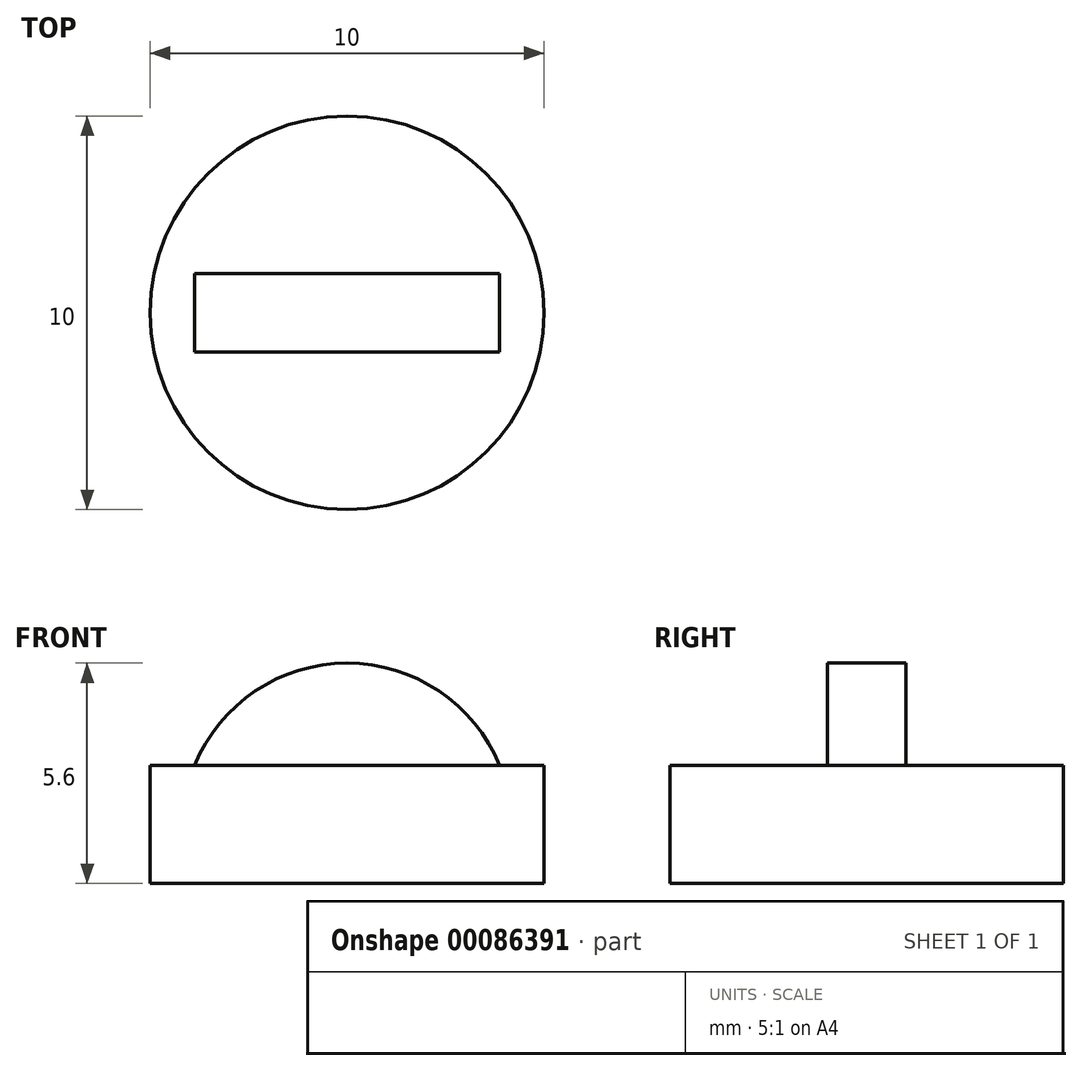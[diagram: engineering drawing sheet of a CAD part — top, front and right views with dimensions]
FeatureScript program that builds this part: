
annotation { "Feature Type Name" : "Feature", "Feature Type Description" : "" }
export const myFeature = defineFeature(function(context is Context, id is Id, definition is map)
    precondition{}
    {
        {
            assignVariable(context, id + "F0", {"name" : "H", "anyValue" : 3});
        }
        {
            var Q0;
            Q0=qCreatedBy(makeId("Top.planeOp"),FACE);
            var sketch = newSketch(context, id + "F1", { "sketchPlane" : qUnion([Q0])});
            skCircle(sketch, "E0", {"center": v(0, 0) * mm, "radius": 5 * mm});
            skCircle(sketch, "E1", {"center": v(0, 0) * mm, "radius": 4 * mm, "construction": true});
            skLineSegment(sketch, "E2.bottom", {"start": v(-3.87, 1) * mm, "end": v(3.87, 1) * mm, "construction": true});
            skLineSegment(sketch, "E2.top", {"start": v(-3.87, -1) * mm, "end": v(3.87, -1) * mm, "construction": true});
            skLineSegment(sketch, "E2.left", {"start": v(-3.87, 1) * mm, "end": v(-3.87, -1) * mm, "construction": true});
            skLineSegment(sketch, "E2.right", {"start": v(3.87, 1) * mm, "end": v(3.87, -1) * mm, "construction": true});
            skSolve(sketch);
        }
        {
            var Q0;
            Q0=makeQuery(id+"F1.imprint","IMPRINT",FACE,{"disambiguationData":[TD([[makeQuery(id+"F1.imprint","IMPRINT",EDGE,{"derivedFrom":sQuery(id+"F1.wireOp",EDGE,"E0")}),1.0]])]});
            extrude(context, id + "F2", {"entities" : qUnion([Q0]), "oppositeDirection" : true, "depth" : (getVariable(context, 'H')) * mm});
        }
        {
            var Q0;
            Q0=qCreatedBy(makeId("Front.planeOp"),FACE);
            var sketch = newSketch(context, id + "F3", { "sketchPlane" : qUnion([Q0])});
            skPoint(sketch, "E3.0", {"position": v(-3.87, 0) * mm});
            skPoint(sketch, "E4.0", {"position": v(3.87, 0) * mm});
            skLineSegment(sketch, "E5.0", {"start": v(-3.87, 0) * mm, "end": v(3.87, 0) * mm});
            skPoint(sketch, "E6.orphan", {"position": v(-5, 0) * mm});
            skPoint(sketch, "E7.orphan", {"position": v(5, 0) * mm});
            skArc(sketch, "E8", {"start": v(3.87, 0) * mm, "mid": v(0, 2.6) * mm, "end": v(-3.87, 0) * mm});
            skSolve(sketch);
        }
        {
            var Q0;
            Q0=makeQuery(id+"F3.imprint","IMPRINT",FACE,{"disambiguationData":[TD([[makeQuery(id+"F3.imprint","IMPRINT",EDGE,{"derivedFrom":sQuery(id+"F3.wireOp",EDGE,"E5.0")}),1.0]])]});
            extrude(context, id + "F4", {"entities" : qUnion([Q0]), "endBound" : BoundingType.SYMMETRIC, "depth" : 2 * mm});
        }
        {
            var Q0;
            Q0=makeQuery(id+"F4.opExtrude","SWEPT_BODY",BODY,{"disambiguationData":[OSD([sQuery(id+"F3.wireOp",EDGE,"E5.0"),sQuery(id+"F3.wireOp",EDGE,"E8")])]});
            transform(context, id + "F5", {"entities" : qUnion([Q0]), "transformType" : TransformType.TRANSLATION_3D, "dx" : 0 * mm, "dy" : 0 * mm, "dz" : (-getVariable(context, 'H')) * mm, "makeCopy" : true});
        }
        {
            var Q0;
            Q0=makeQuery(id+"F5.opPattern","COPY",FACE,{"derivedFrom":makeQuery(id+"F4.opExtrude","SWEPT_FACE",FACE,{"disambiguationData":[OSD([sQuery(id+"F3.wireOp",EDGE,"E5.0")])]}),"instanceName":"1"});
            var sketch = newSketch(context, id + "F6", { "sketchPlane" : qUnion([Q0])});
            skLineSegment(sketch, "E9", {"start": v(0, 1) * mm, "end": v(0, -1) * mm, "construction": true});
            skPoint(sketch, "E10", {"position": v(0, 0) * mm});
            skSolve(sketch);
        }
        {
            var Q0;
            Q0=makeQuery(id+"F5.opPattern","COPY",BODY,{"derivedFrom":makeQuery(id+"F4.opExtrude","SWEPT_BODY",BODY,{"disambiguationData":[OSD([sQuery(id+"F3.wireOp",EDGE,"E5.0"),sQuery(id+"F3.wireOp",EDGE,"E8")])]}),"instanceName":"1"});
            var Q1;
            Q1=sQuery(id+"F6.wireOp",VERTEX,"E10");
            transform(context, id + "F7", {"entities" : qUnion([Q0]), "transformType" : TransformType.SCALE_UNIFORMLY, "scale" : 1.15, "scalePoint" : qUnion([Q1]), "makeCopy" : false});
        }
        {
            var Q0;
            Q0=makeQuery(id+"F5.opPattern","COPY",BODY,{"derivedFrom":makeQuery(id+"F4.opExtrude","SWEPT_BODY",BODY,{"disambiguationData":[OSD([sQuery(id+"F3.wireOp",EDGE,"E5.0"),sQuery(id+"F3.wireOp",EDGE,"E8")])]}),"instanceName":"1"});
            var Q1;
            Q1=makeQuery(id+"F4.opExtrude","SWEPT_BODY",BODY,{"disambiguationData":[OSD([sQuery(id+"F3.wireOp",EDGE,"E5.0"),sQuery(id+"F3.wireOp",EDGE,"E8")])]});
            booleanBodies(context, id + "F8", {"operationType" : BooleanOperationType.SUBTRACTION, "tools" : qUnion([Q0]), "targets" : qUnion([Q1])});
        }
    });
